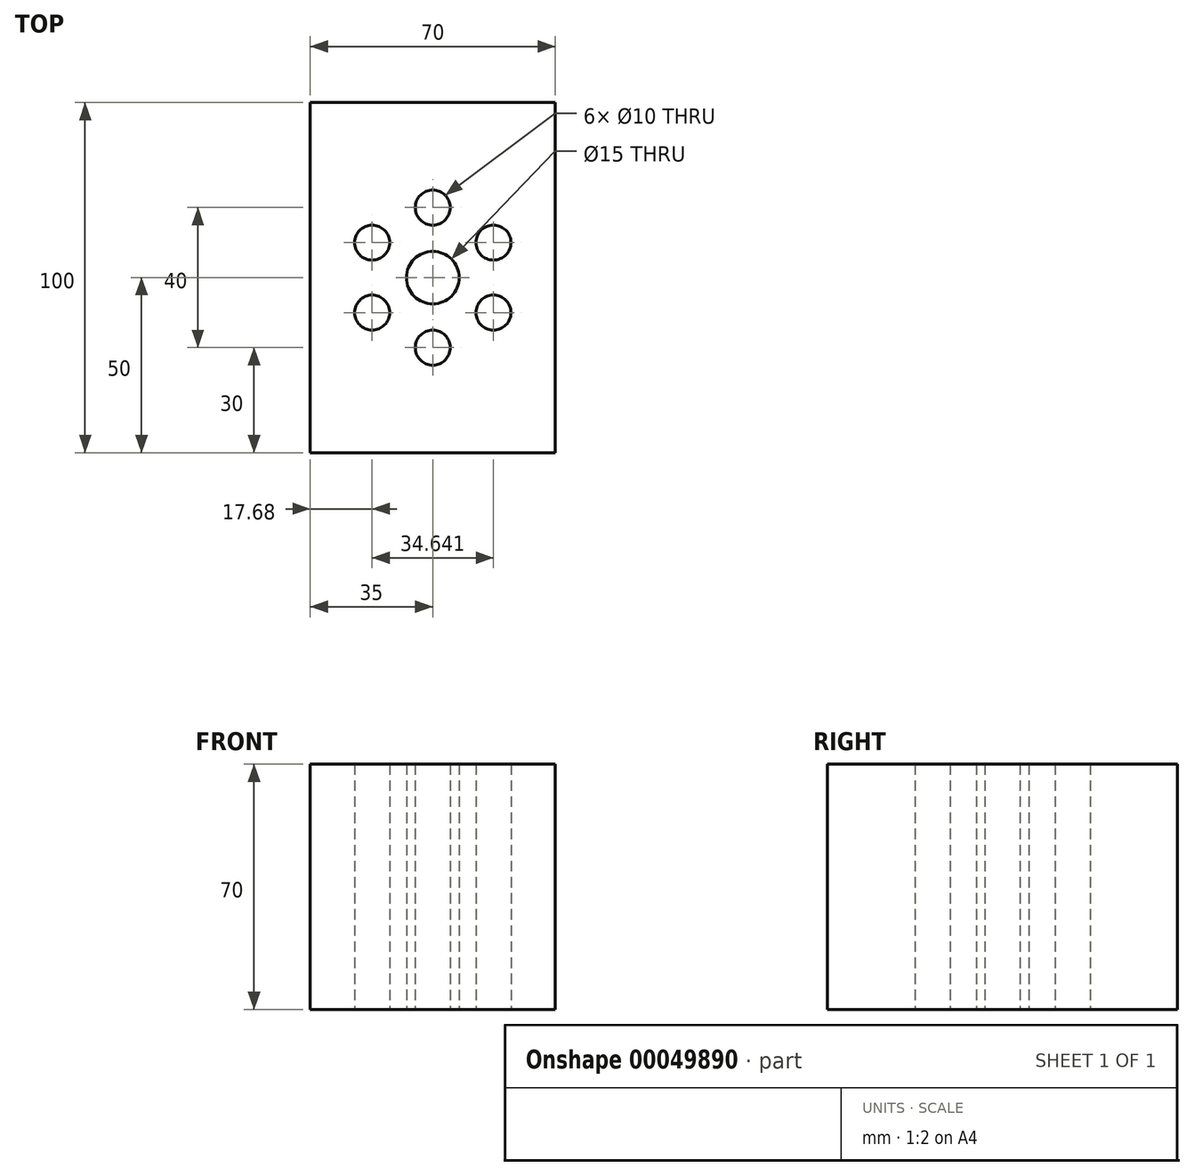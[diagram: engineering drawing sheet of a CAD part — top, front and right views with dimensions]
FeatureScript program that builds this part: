
annotation { "Feature Type Name" : "Feature", "Feature Type Description" : "" }
export const myFeature = defineFeature(function(context is Context, id is Id, definition is map)
    precondition{}
    {
        {
            var Q0;
            Q0=qCreatedBy(makeId("Top.planeOp"),FACE);
            var sketch = newSketch(context, id + "F0", { "sketchPlane" : qUnion([Q0])});
            skCircle(sketch, "E0", {"center": v(0, 0) * mm, "radius": 7.5 * mm});
            skCircle(sketch, "E1", {"center": v(0, 20) * mm, "radius": 5 * mm});
            skCircle(sketch, "E2", {"center": v(17.32, 10) * mm, "radius": 5 * mm});
            skCircle(sketch, "E3", {"center": v(-17.32, 10) * mm, "radius": 5 * mm});
            skCircle(sketch, "E4.MirrorC", {"center": v(-17.32, -10) * mm, "radius": 5 * mm});
            skCircle(sketch, "E5.MirrorC", {"center": v(0, -20) * mm, "radius": 5 * mm});
            skCircle(sketch, "E6.MirrorC", {"center": v(17.32, -10) * mm, "radius": 5 * mm});
            skLineSegment(sketch, "E7.bottom", {"start": v(-35, 50) * mm, "end": v(35, 50) * mm});
            skLineSegment(sketch, "E7.top", {"start": v(-35, -50) * mm, "end": v(35, -50) * mm});
            skLineSegment(sketch, "E7.left", {"start": v(-35, 50) * mm, "end": v(-35, -50) * mm});
            skLineSegment(sketch, "E7.right", {"start": v(35, 50) * mm, "end": v(35, -50) * mm});
            skSolve(sketch);
        }
        {
            var Q0;
            Q0=makeQuery(id+"F0.imprint","IMPRINT",FACE,{"disambiguationData":[TD([[makeQuery(id+"F0.imprint","IMPRINT",EDGE,{"derivedFrom":sQuery(id+"F0.wireOp",EDGE,"E0")}),-1.0]])]});
            extrude(context, id + "F1", {"entities" : qUnion([Q0]), "depth" : 70 * mm});
        }
    });
